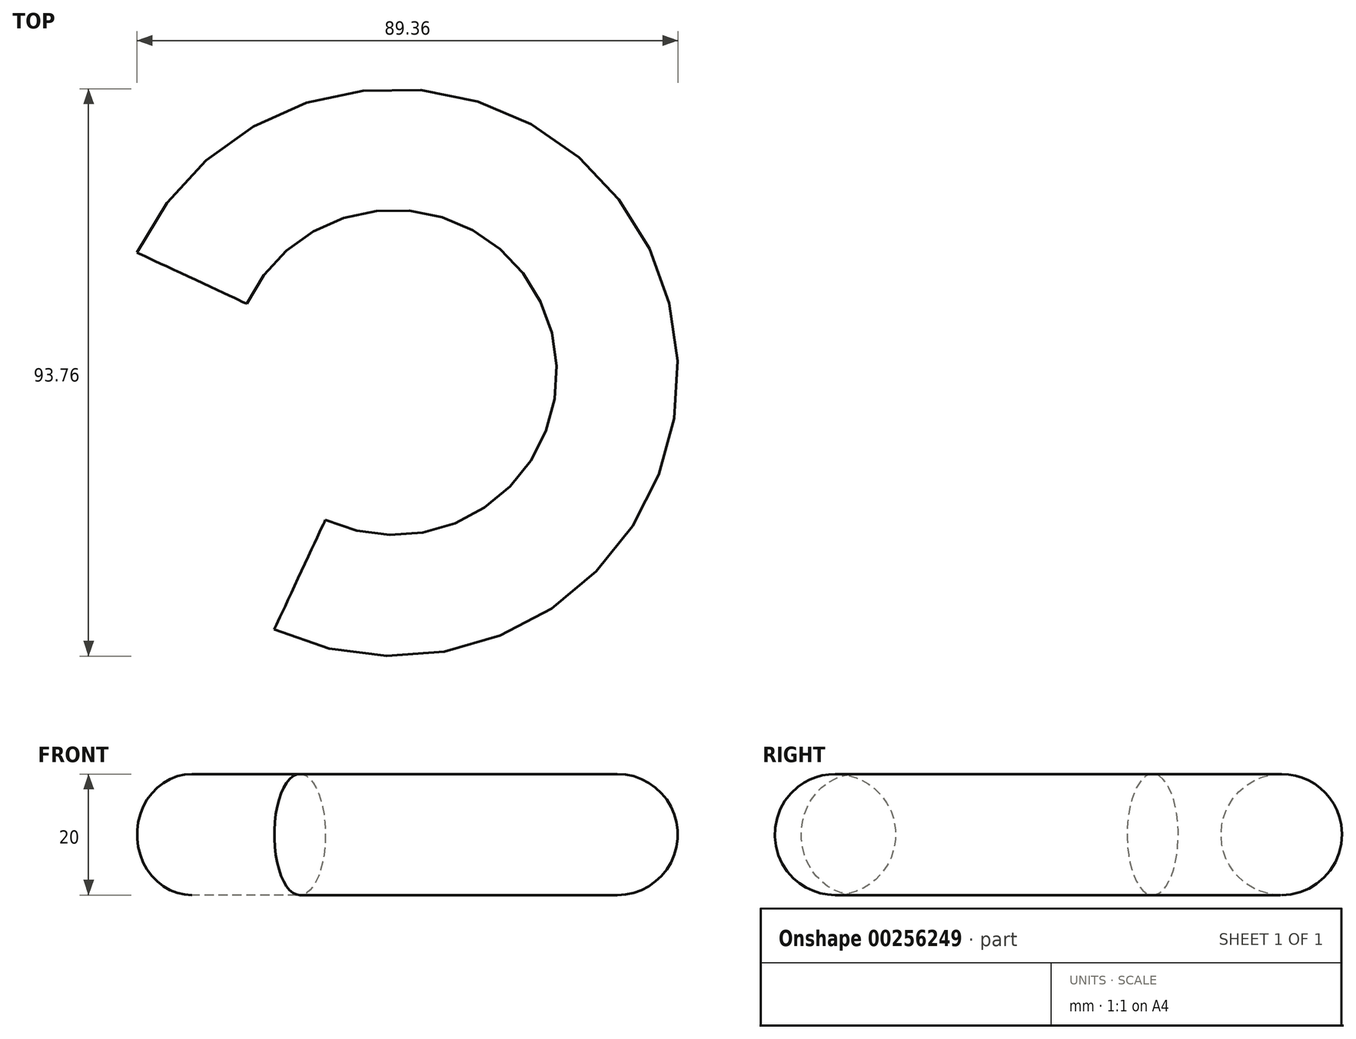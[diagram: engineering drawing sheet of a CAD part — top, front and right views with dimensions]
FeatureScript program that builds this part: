
annotation { "Feature Type Name" : "Feature", "Feature Type Description" : "" }
export const myFeature = defineFeature(function(context is Context, id is Id, definition is map)
    precondition{}
    {
        {
            var Q0;
            Q0=qCreatedBy(makeId("Front.planeOp"),FACE);
            var sketch = newSketch(context, id + "F0", { "sketchPlane" : qUnion([Q0])});
            skCircle(sketch, "E0", {"center": v(36.88, 0) * mm, "radius": 10 * mm});
            skLineSegment(sketch, "E1", {"start": v(0, 33.3) * mm, "end": v(0, -39.26) * mm, "construction": true});
            skSolve(sketch);
        }
        {
            var Q0;
            Q0=makeQuery(id+"F0.imprint","IMPRINT",FACE,{"disambiguationData":[TD([[makeQuery(id+"F0.imprint","IMPRINT",EDGE,{"derivedFrom":sQuery(id+"F0.wireOp",EDGE,"E0")}),1.0]])]});
            var Q1;
            Q1=sQuery(id+"F0.wireOp",EDGE,"E1");
            revolve(context, id + "F1", {"entities" : qUnion([Q0]), "axis" : qUnion([Q1]), "revolveType" : RevolveType.TWO_DIRECTIONS, "angle" : 115 * degree, "angleBack" : 205 * degree});
        }
    });
